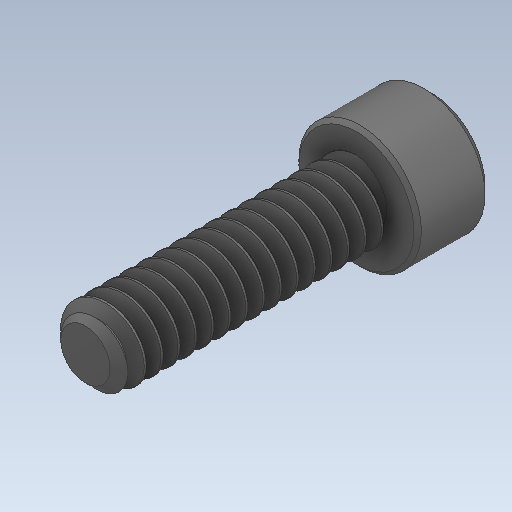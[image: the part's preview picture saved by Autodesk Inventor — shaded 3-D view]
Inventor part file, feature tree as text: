
AUTODESK INVENTOR PART (.ipt)
format: ipt  version: 2020 (Build 240168000, 168)  size: 654,848 bytes
history: native  units: in
note: dims shown in document units (in); Inventor stores cm internally (conversion verified against a paired STEP export)
features: chamfer x1
ambient origin geometry x8: Origin, YZ Plane, XZ Plane, XY Plane, X Axis, Y Axis, Z Axis, Center Point
bodies: Solid1 (feature_tree)
feature tree (1):
  chamfer  "Chamfer2"  [1 undecoded]
note: 1 required parameter value undecoded (feature->parameter linkage not recoverable at this tier; creation-order binding heuristic only, values carry confidence <= 0.55)
